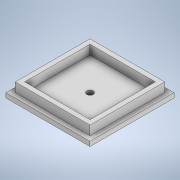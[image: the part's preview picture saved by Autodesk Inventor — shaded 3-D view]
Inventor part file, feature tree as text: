
AUTODESK INVENTOR PART (.ipt)
format: ipt  version: 2020 (Build 240168000, 168)  size: 128,000 bytes
history: native  units: in
note: dims shown in document units (in); Inventor stores cm internally (conversion verified against a paired STEP export)
features: extrude x3, sketch x3
ambient origin geometry x8: Origin, YZ Plane, XZ Plane, XY Plane, X Axis, Y Axis, Z Axis, Center Point
bodies: Solid1 (feature_tree)
feature tree (6):
  extrude  "Extrusion1"  Depth=3.5433in
  extrude  "Extrusion2"  Depth=0.1969in
  extrude  "Extrusion3"  Depth=3.1496in
  sketch  "Sketch1"  dims[d0=3.5433in d1=3.5433in]
  sketch  "Sketch2"  dims[d2=0.1969in d3=0.0in d4=0.1969in]
  sketch  "Sketch3"  dims[d5=0.1969in d6=3.1496in d7=3.1496in d8=0.1969in d9=0.1969in d10=2.7559in d11=2.7559in d12=0.3937in d13=0.0in d14=1.7717in d15=1.7717in d16=0.2756in d17=0.3937in d18=0.0in]
